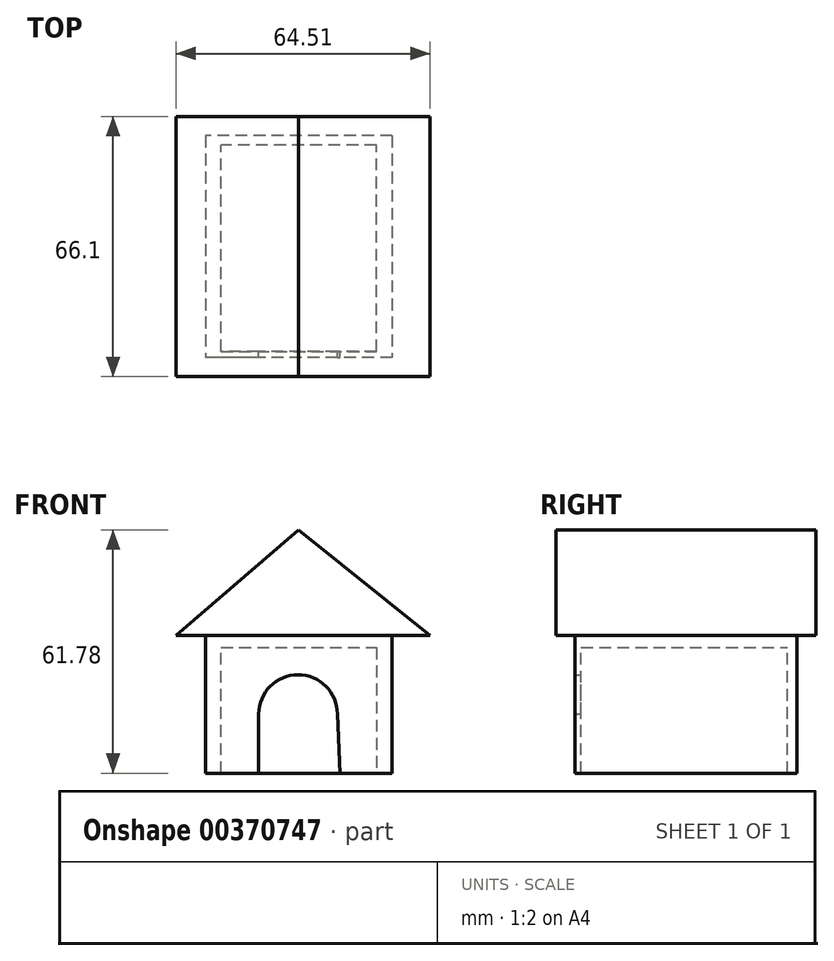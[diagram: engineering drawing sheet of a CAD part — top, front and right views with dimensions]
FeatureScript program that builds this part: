
annotation { "Feature Type Name" : "Feature", "Feature Type Description" : "" }
export const myFeature = defineFeature(function(context is Context, id is Id, definition is map)
    precondition{}
    {
        {
            var Q0;
            Q0=qCreatedBy(makeId("Top.planeOp"),FACE);
            var sketch = newSketch(context, id + "F0", { "sketchPlane" : qUnion([Q0])});
            skLineSegment(sketch, "E0.bottom", {"start": v(23.72, 28.23) * mm, "end": v(-23.72, 28.23) * mm});
            skLineSegment(sketch, "E0.top", {"start": v(23.72, -28.23) * mm, "end": v(-23.72, -28.23) * mm});
            skLineSegment(sketch, "E0.left", {"start": v(23.72, 28.23) * mm, "end": v(23.72, -28.23) * mm});
            skLineSegment(sketch, "E0.right", {"start": v(-23.72, 28.23) * mm, "end": v(-23.72, -28.23) * mm});
            skPoint(sketch, "E0.middle", {"position": v(0, 0) * mm});
            skSolve(sketch);
        }
        {
            var Q0;
            Q0 = qSketchRegion(id + "F0", true);
            extrude(context, id + "F1", {"entities" : qUnion([Q0]), "depth" : 40 * mm});
        }
        {
            var Q0;
            Q0=qCreatedBy(makeId("Front.planeOp"),FACE);
            var sketch = newSketch(context, id + "F2", { "sketchPlane" : qUnion([Q0])});
            skLineSegment(sketch, "E1", {"start": v(0, 61.78) * mm, "end": v(-31.17, 34.95) * mm});
            skLineSegment(sketch, "E2", {"start": v(33.34, 34.95) * mm, "end": v(0, 61.78) * mm});
            skLineSegment(sketch, "E3", {"start": v(-31.17, 34.95) * mm, "end": v(-28.1, 34.95) * mm});
            skLineSegment(sketch, "E4", {"start": v(29.81, 34.95) * mm, "end": v(33.34, 34.95) * mm});
            skLineSegment(sketch, "E5", {"start": v(-31.17, 34.95) * mm, "end": v(33.34, 34.95) * mm});
            skSolve(sketch);
        }
        {
            var Q0;
            Q0 = qSketchRegion(id + "F2", true);
            extrude(context, id + "F3", {"entities" : qUnion([Q0]), "operationType" : NewBodyOperationType.ADD, "depth" : 33 * mm, "hasSecondDirection" : true, "secondDirectionOppositeDirection" : true, "secondDirectionDepth" : 33.1 * mm});
        }
        {
            var Q0;
            Q0=qCreatedBy(makeId("Front.planeOp"),FACE);
            var sketch = newSketch(context, id + "F4", { "sketchPlane" : qUnion([Q0])});
            skArc(sketch, "E6", {"start": v(9.84, 15) * mm, "mid": v(-0.16, 25) * mm, "end": v(-10.16, 15) * mm});
            skLineSegment(sketch, "E7", {"start": v(-10.16, 15) * mm, "end": v(-10.16, 0) * mm});
            skLineSegment(sketch, "E8", {"start": v(-10.16, 0) * mm, "end": v(10.5, 0) * mm});
            skLineSegment(sketch, "E9", {"start": v(10.5, 0) * mm, "end": v(9.84, 15) * mm});
            skSolve(sketch);
        }
        {
            var Q0;
            Q0 = qSketchRegion(id + "F4", true);
            extrude(context, id + "F5", {"entities" : qUnion([Q0]), "operationType" : NewBodyOperationType.REMOVE, "depth" : 33.3 * mm});
        }
        {
            var Q0;
            Q0=qCreatedBy(makeId("Front.planeOp"),FACE);
            var sketch = newSketch(context, id + "F6", { "sketchPlane" : qUnion([Q0])});
            skLineSegment(sketch, "E10", {"start": v(-19.72, 0) * mm, "end": v(-19.72, 31.95) * mm});
            skLineSegment(sketch, "E11", {"start": v(-19.72, 31.95) * mm, "end": v(19.72, 31.95) * mm});
            skLineSegment(sketch, "E12", {"start": v(19.72, 31.95) * mm, "end": v(19.72, 0) * mm});
            skLineSegment(sketch, "E13", {"start": v(19.72, 0) * mm, "end": v(-19.72, 0) * mm});
            skSolve(sketch);
        }
        {
            var Q0;
            Q0 = qSketchRegion(id + "F6", true);
            extrude(context, id + "F7", {"entities" : qUnion([Q0]), "operationType" : NewBodyOperationType.REMOVE, "depth" : 26.6 * mm, "hasSecondDirection" : true, "secondDirectionOppositeDirection" : true, "secondDirectionDepth" : 25.8 * mm});
        }
    });
